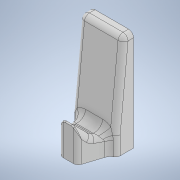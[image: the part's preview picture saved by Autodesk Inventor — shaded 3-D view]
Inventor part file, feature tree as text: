
AUTODESK INVENTOR PART (.ipt)
format: ipt  version: 2022 (Build 260153000, 153)  size: 297,472 bytes
history: native  units: mm
features: extrude x4, fillet x3, sketch x3
ambient origin geometry x8: Origin, YZ Plane, XZ Plane, XY Plane, X Axis, Y Axis, Z Axis, Center Point
bodies: Solid1 (feature_tree)
feature tree (10):
  extrude  "Extrusion1"  Depth=26.0mm
  extrude  "Extrusion2"  Depth=13.0mm
  extrude  "Extrusion3"  Depth=5.0mm
  fillet  "Fillet2"  Radius=11.0mm
  extrude  "Extrusion4"  Depth=5.0mm
  fillet  "Fillet3"  Radius=11.0mm
  fillet  "Fillet4"  Radius=12.0mm
  sketch  "Sketch1"  dims[d0=26.0mm d1=26.0mm]
  sketch  "Sketch2"  dims[d2=13.0mm d3=13.0mm]
  sketch  "Sketch4"  dims[d4=60.0mm d5=0.0mm d12=6.0mm d13=11.0mm d14=18.0mm d15=11.0mm d16=12.0mm d17=20.0mm d18=60.0mm d19=0.0mm d21=33.0mm d22=40.0mm d23=3.0mm d24=3.0mm d25=60.0mm d26=0.0mm d28=0.5mm d29=3.0mm d30=2.0mm d31=2.0mm d32=3.0mm d33=0.0mm d34=10.0mm d35=11.0mm d36=3.0mm d37=3.0mm d38=3.0mm d39=5.0mm]
